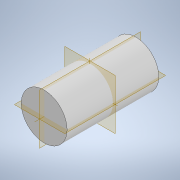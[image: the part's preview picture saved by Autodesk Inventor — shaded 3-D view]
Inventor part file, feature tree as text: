
AUTODESK INVENTOR PART (.ipt)
format: ipt  version: 2022.4 (Build 264492010, 492A)  size: 95,232 bytes
history: native  units: mm
features: extrude x1, sketch x1
ambient origin geometry x8: Origin, YZ Plane, XZ Plane, XY Plane, X Axis, Y Axis, Z Axis, Center Point
bodies: Solid1 (feature_tree)
feature tree (2):
  extrude  "Extrusion1"  Depth=10.0mm TaperAngle=0.0deg
  sketch  "Sketch1"  dims[d0=5.0mm d1=10.0mm d2=0.0mm]
